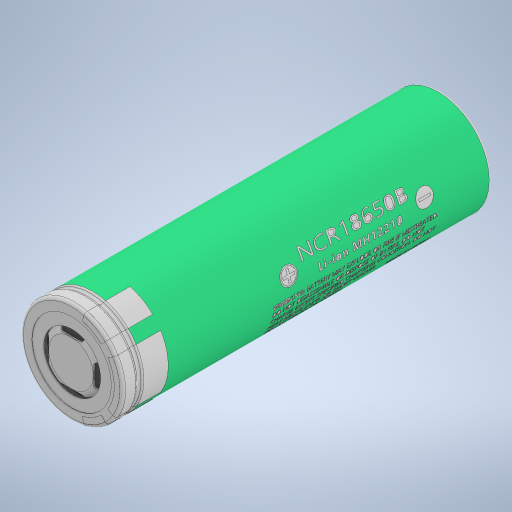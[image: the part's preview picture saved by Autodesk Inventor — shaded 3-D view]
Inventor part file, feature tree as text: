
AUTODESK INVENTOR PART (.ipt)
format: ipt  version: 2024 (Build 280153000, 153)  size: 12,150,272 bytes
history: native  units: mm
features: other x6, revolve x2
ambient origin geometry x8: Origin, YZ Plane, XZ Plane, XY Plane, X Axis, Y Axis, Z Axis, Center Point
bodies: Solide1 (feature_tree), Solide2 (feature_tree), Solide3 (feature_tree), Solide4 (feature_tree), Solide5 (feature_tree), Solide6 (feature_tree), Solide7 (feature_tree)
feature tree (8):
  other  "Bateria 18650 Panasonic.STEP"
  other  "Envolver1"
  revolve  "Revolución3"  [1 undecoded]
  revolve  "Revolución4"  [1 undecoded]
  other  "Cortar-Extruir1"
  other  "Cortar-Extruir3[1]"
  other  "Cortar-Extruir3[2]"
  other  "Cortar-Extruir3[3]"
note: 2 required parameter values undecoded (feature->parameter linkage not recoverable at this tier; creation-order binding heuristic only, values carry confidence <= 0.55)
